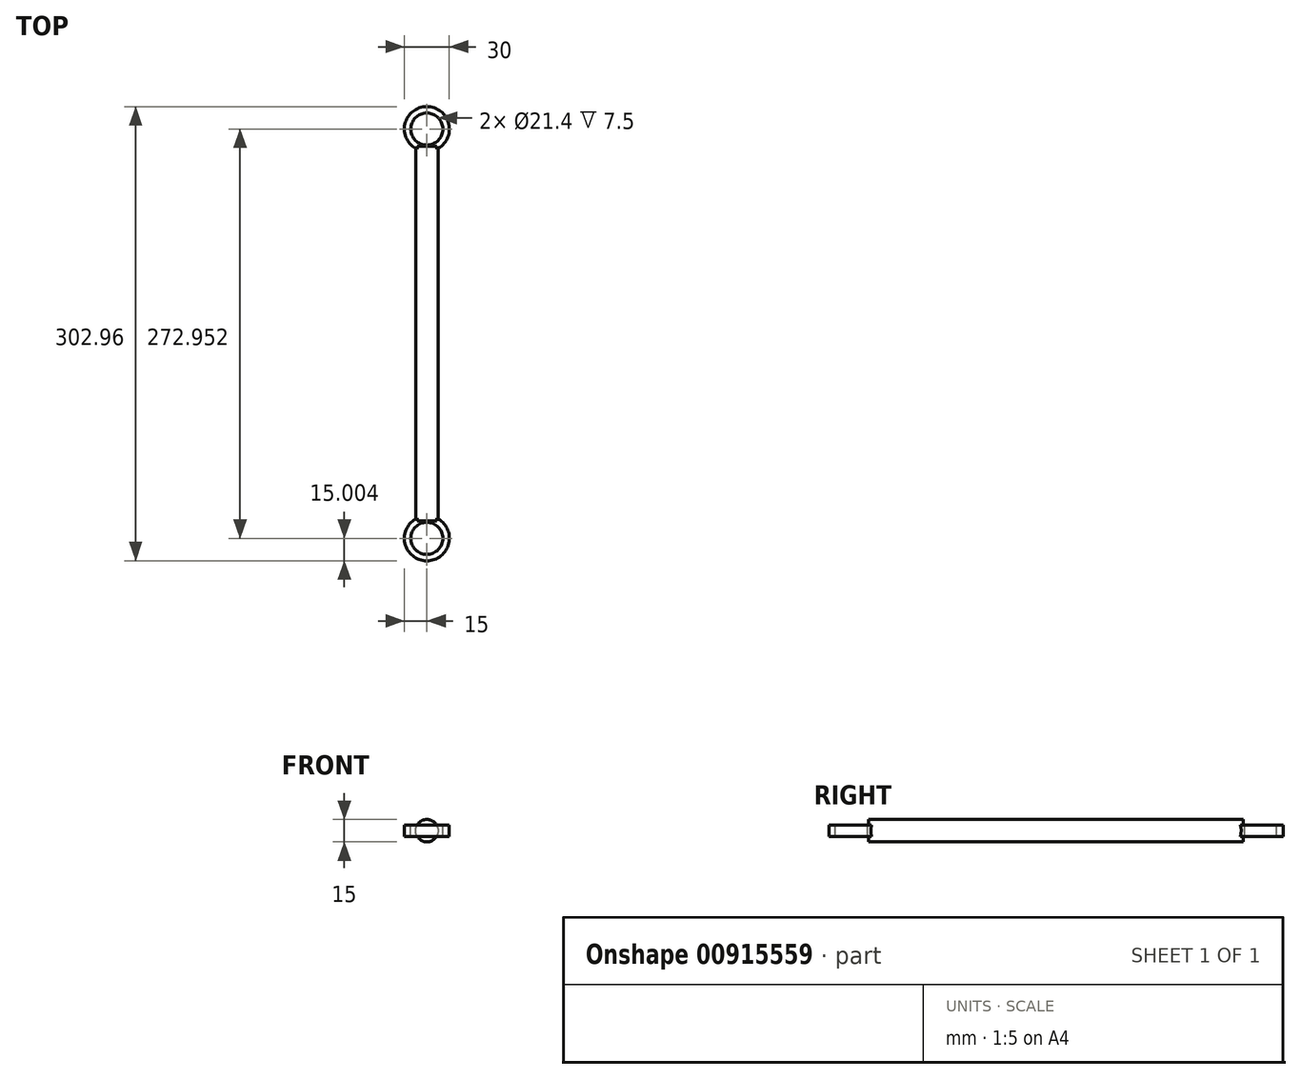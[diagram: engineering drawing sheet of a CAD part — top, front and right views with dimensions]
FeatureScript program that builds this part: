
annotation { "Feature Type Name" : "Feature", "Feature Type Description" : "" }
export const myFeature = defineFeature(function(context is Context, id is Id, definition is map)
    precondition{}
    {
        {
            var Q0;
            Q0=qCreatedBy(makeId("Front.planeOp"),FACE);
            var sketch = newSketch(context, id + "F0", { "sketchPlane" : qUnion([Q0])});
            skCircle(sketch, "E0", {"center": v(0, 0) * mm, "radius": 7.5 * mm});
            skSolve(sketch);
        }
        {
            var Q0;
            Q0=makeQuery(id+"F0.imprint","IMPRINT",FACE,{"disambiguationData":[TD([[makeQuery(id+"F0.imprint","IMPRINT",EDGE,{"derivedFrom":sQuery(id+"F0.wireOp",EDGE,"E0")}),1.0]])]});
            extrude(context, id + "F1", {"entities" : qUnion([Q0]), "depth" : 125 * mm, "offsetDistance" : 25 * mm});
        }
        {
            var Q0;
            Q0=qCreatedBy(makeId("Top.planeOp"),FACE);
            var sketch = newSketch(context, id + "F2", { "sketchPlane" : qUnion([Q0])});
            skCircle(sketch, "E1", {"center": v(0, -136.48) * mm, "radius": 15 * mm});
            skCircle(sketch, "E2", {"center": v(0, -136.48) * mm, "radius": 10.7 * mm});
            skSolve(sketch);
        }
        {
            var Q0;
            Q0=makeQuery(id+"F2.imprint","IMPRINT",FACE,{"disambiguationData":[TD([[makeQuery(id+"F2.imprint","IMPRINT",EDGE,{"derivedFrom":sQuery(id+"F2.wireOp",EDGE,"E1")}),1.0]])]});
            extrude(context, id + "F3", {"entities" : qUnion([Q0]), "operationType" : NewBodyOperationType.ADD, "endBound" : BoundingType.SYMMETRIC, "oppositeDirection" : true, "depth" : 7.5 * mm, "offsetDistance" : 25 * mm});
        }
        {
            var Q0;
            Q0=makeQuery(id+"F1.opExtrude","SWEPT_BODY",BODY,{"disambiguationData":[OSD([sQuery(id+"F0.wireOp",EDGE,"E0")])]});
            var Q1;
            Q1=qCreatedBy(makeId("Front.planeOp"),FACE);
            mirror(context, id + "F4", {"operationType" : NewBodyOperationType.ADD, "entities" : qUnion([Q0]), "mirrorPlane" : qUnion([Q1])});
        }
    });
